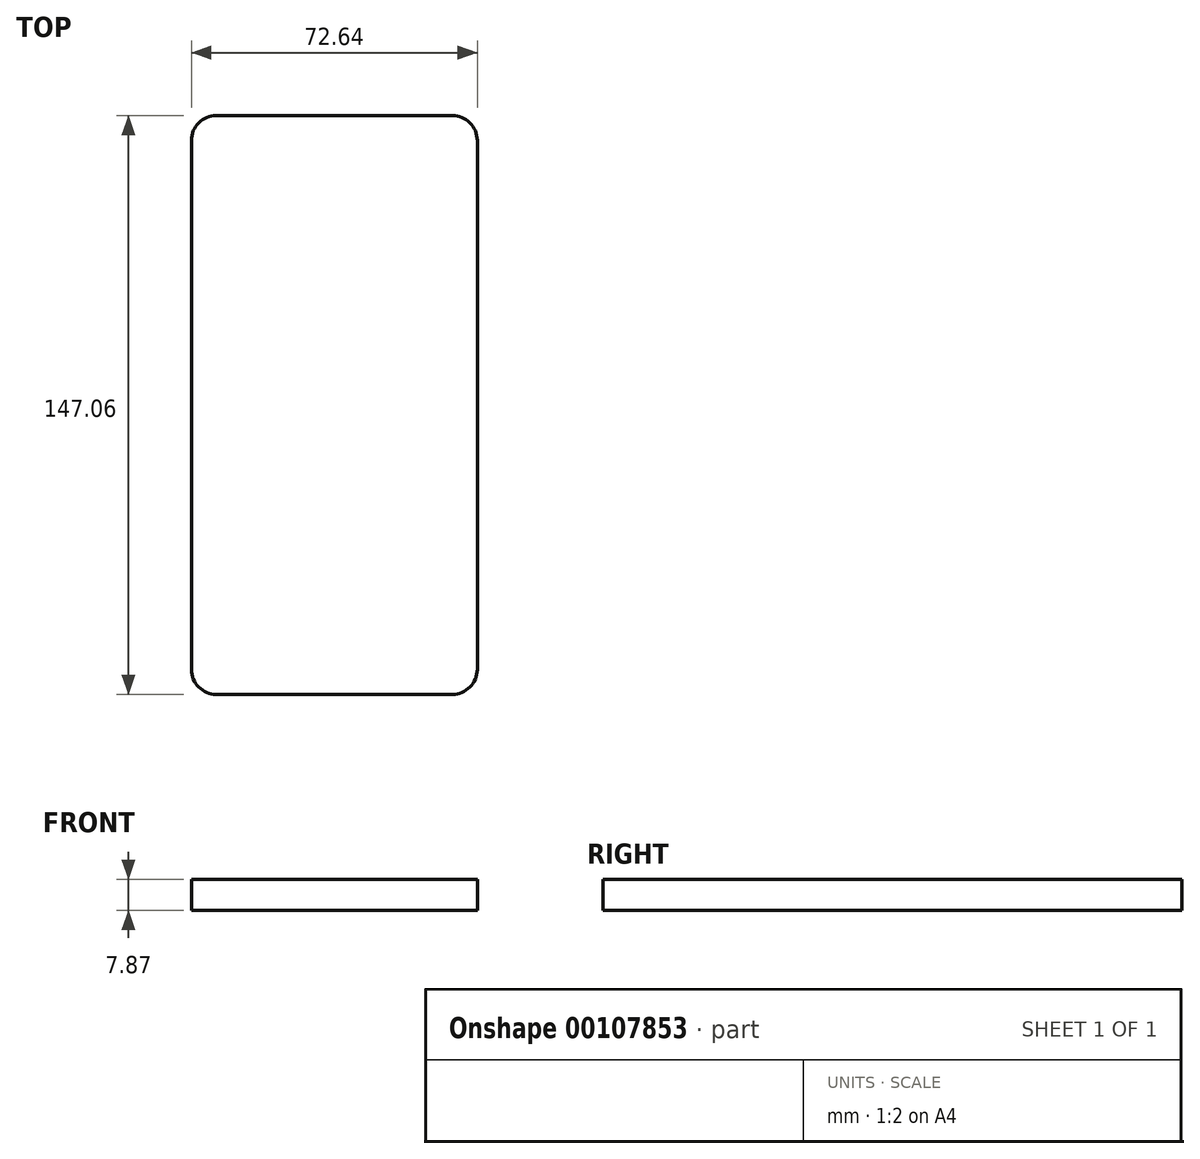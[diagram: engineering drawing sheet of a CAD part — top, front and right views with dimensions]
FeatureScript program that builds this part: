
annotation { "Feature Type Name" : "Feature", "Feature Type Description" : "" }
export const myFeature = defineFeature(function(context is Context, id is Id, definition is map)
    precondition{}
    {
        {
            var Q0;
            Q0=qCreatedBy(makeId("Top.planeOp"),FACE);
            var sketch = newSketch(context, id + "F0", { "sketchPlane" : qUnion([Q0])});
            skLineSegment(sketch, "E0.bottom", {"start": v(-30.42, 114.2) * mm, "end": v(29.52, 114.2) * mm});
            skLineSegment(sketch, "E0.top", {"start": v(-30.42, -32.86) * mm, "end": v(29.52, -32.86) * mm});
            skLineSegment(sketch, "E0.left", {"start": v(-36.77, 107.85) * mm, "end": v(-36.77, -26.51) * mm});
            skLineSegment(sketch, "E0.right", {"start": v(35.87, 107.85) * mm, "end": v(35.87, -26.51) * mm});
            skPoint(sketch, "E1.visualSharp", {"position": v(-36.77, 114.2) * mm});
            skArc(sketch, "E1.filletArc", {"start": v(-30.42, 114.2) * mm, "mid": v(-34.91, 112.34) * mm, "end": v(-36.77, 107.85) * mm});
            skPoint(sketch, "E2.visualSharp", {"position": v(35.87, 114.2) * mm});
            skArc(sketch, "E2.filletArc", {"start": v(35.87, 107.85) * mm, "mid": v(34.01, 112.34) * mm, "end": v(29.52, 114.2) * mm});
            skPoint(sketch, "E3.visualSharp", {"position": v(35.87, -32.86) * mm});
            skArc(sketch, "E3.filletArc", {"start": v(29.52, -32.86) * mm, "mid": v(34.01, -31) * mm, "end": v(35.87, -26.51) * mm});
            skPoint(sketch, "E4.visualSharp", {"position": v(-36.77, -32.86) * mm});
            skArc(sketch, "E4.filletArc", {"start": v(-36.77, -26.51) * mm, "mid": v(-34.91, -31) * mm, "end": v(-30.42, -32.86) * mm});
            skSolve(sketch);
        }
        {
            var Q0;
            Q0=makeQuery(id+"F0.imprint","IMPRINT",FACE,{"disambiguationData":[TD([[makeQuery(id+"F0.imprint","IMPRINT",EDGE,{"derivedFrom":sQuery(id+"F0.wireOp",EDGE,"E0.bottom")}),-1.0]])]});
            extrude(context, id + "F1", {"entities" : qUnion([Q0]), "depth" : 7.87 * mm});
        }
    });
